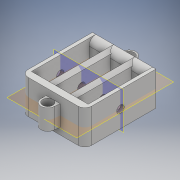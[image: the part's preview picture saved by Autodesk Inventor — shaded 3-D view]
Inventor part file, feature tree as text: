
AUTODESK INVENTOR PART (.ipt)
format: ipt  version: 2018 (Build 220112000, 112)  size: 243,712 bytes
history: native  units: mm
features: sketch x6, extrude x4, fillet x3, plane x2, mirror x2, hole x1, chamfer x1, projected_geometry x1
ambient origin geometry x8: Origin, YZ Plane, XZ Plane, XY Plane, X Axis, Y Axis, Z Axis, Center Point
bodies: Solid1 (feature_tree)
feature tree (20):
  extrude  "Extrusion1"  Depth=17.0mm
  hole  "Hole1"  [1 undecoded]
  fillet  "Fillet1"  Radius=10.0mm
  fillet  "Fillet2"  Radius=2.0mm
  extrude  "Extrusion2"  Depth=10.0mm TaperAngle=0.0deg
  fillet  "Fillet3"  Radius=2.0mm
  sketch  "Sketch4"  dims[d20=2.0mm d21=10.0mm d22=0.0mm d23=2.0mm]
  extrude  "Extrusion4"  Depth=1.5mm
  sketch  "Sketch7"  dims[d29=4.0mm d30=10.0mm d31=0.0mm d32=2.0mm d33=0.0mm d34=1.0mm d35=2.0mm d36=45.0deg]
  plane  "Work Plane1"
  extrude  "Extrusion5"  Depth=10.0mm TaperAngle=0.0deg
  mirror  "Mirror1"
  plane  "Work Plane2"
  mirror  "Mirror2"
  chamfer  "Chamfer1"  Distance=2.0mm
  sketch  "Sketch1"  dims[d0=4.25mm d1=17.0mm]
  sketch  "Sketch2"  dims[d2=2.0mm d3=40.0mm d5=6.25mm d6=10.0mm d8=10.0mm d10=10.0mm d11=0.0mm]
  sketch  "Sketch3"  dims[d12=2.2mm d13=6.0mm d14=4.0mm d15=2.0mm d16=90.0deg d17=8.0mm d18=20.594885mm d19=2.0mm]
  sketch  "Sketch6"  dims[d27=3.0mm d28=1.5mm]
  projected_geometry  "Projected Loop1"
note: 1 required parameter value undecoded (feature->parameter linkage not recoverable at this tier; creation-order binding heuristic only, values carry confidence <= 0.55)
